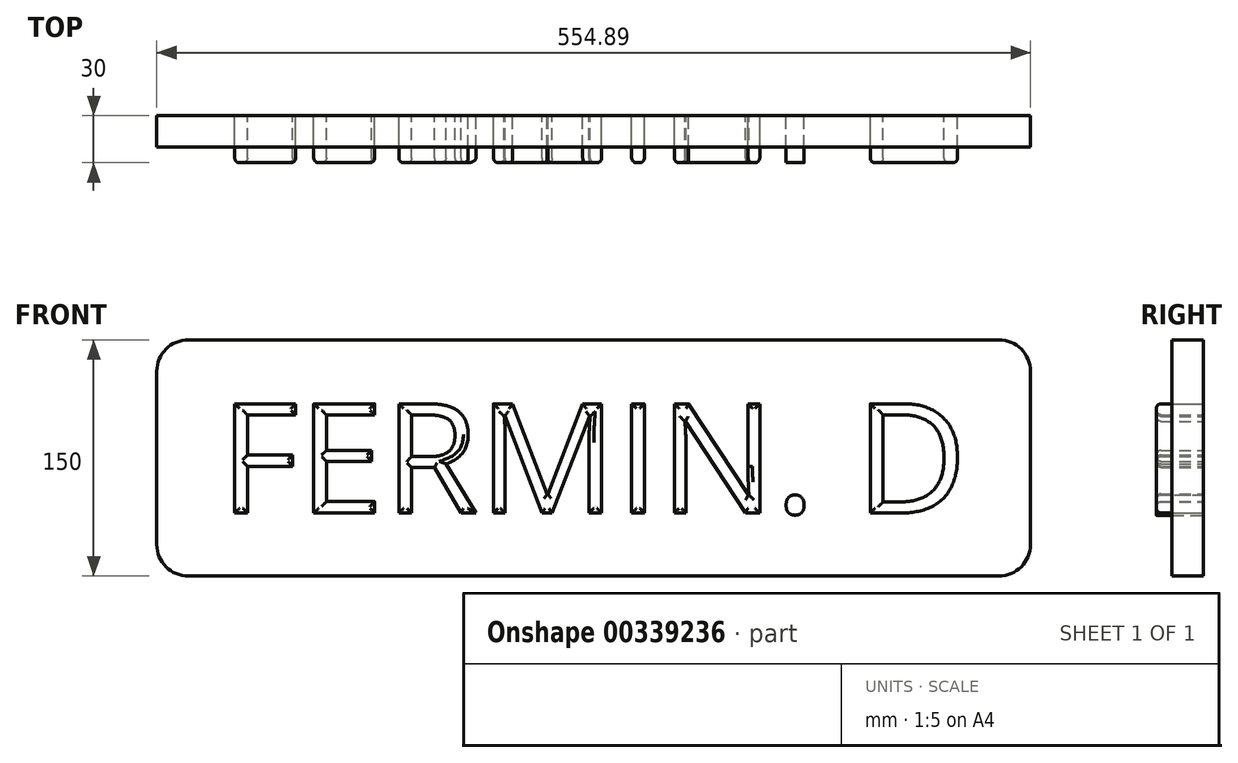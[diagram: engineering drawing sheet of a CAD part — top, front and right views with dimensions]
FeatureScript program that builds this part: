
annotation { "Feature Type Name" : "Feature", "Feature Type Description" : "" }
export const myFeature = defineFeature(function(context is Context, id is Id, definition is map)
    precondition{}
    {
        {
            var Q0;
            Q0=qCreatedBy(makeId("Front.planeOp"),FACE);
            var sketch = newSketch(context, id + "F0", { "sketchPlane" : qUnion([Q0])});
            skText(sketch, "E0", { "text": "FERMIN. D", "fontName": "OpenSans-Regular.ttf"});
            const initialGuessF0  = {"E0": [0.29518, 0.37068, 1, 0, 0.07]};
            skSetInitialGuess(sketch, initialGuessF0);
            skSolve(sketch);
        }
        {
            var Q0;
            Q0=qCreatedBy(makeId("Front.planeOp"),FACE);
            var sketch = newSketch(context, id + "F1", { "sketchPlane" : qUnion([Q0])});
            skLineSegment(sketch, "E1.0", {"start": v(295.18, 440.68) * mm, "end": v(770.07, 440.68) * mm, "construction": true});
            skLineSegment(sketch, "E2.0", {"start": v(295.18, 370.68) * mm, "end": v(770.07, 370.68) * mm, "construction": true});
            skLineSegment(sketch, "E3.0", {"start": v(770.07, 370.68) * mm, "end": v(770.07, 440.68) * mm, "construction": true});
            skLineSegment(sketch, "E4.0", {"start": v(295.18, 370.68) * mm, "end": v(295.18, 440.68) * mm, "construction": true});
            skLineSegment(sketch, "E5.0", {"start": v(275.18, 480.68) * mm, "end": v(790.07, 480.68) * mm});
            skLineSegment(sketch, "E5.1", {"start": v(255.18, 350.68) * mm, "end": v(255.18, 460.68) * mm});
            skLineSegment(sketch, "E5.2", {"start": v(275.18, 330.68) * mm, "end": v(790.07, 330.68) * mm});
            skLineSegment(sketch, "E5.3", {"start": v(810.07, 350.68) * mm, "end": v(810.07, 460.68) * mm});
            skPoint(sketch, "E6.visualSharp", {"position": v(255.18, 480.68) * mm});
            skArc(sketch, "E6.filletArc", {"start": v(275.18, 480.68) * mm, "mid": v(261.04, 474.82) * mm, "end": v(255.18, 460.68) * mm});
            skPoint(sketch, "E7.visualSharp", {"position": v(810.07, 480.68) * mm});
            skArc(sketch, "E7.filletArc", {"start": v(810.07, 460.68) * mm, "mid": v(804.21, 474.82) * mm, "end": v(790.07, 480.68) * mm});
            skPoint(sketch, "E8.visualSharp", {"position": v(810.07, 330.68) * mm});
            skArc(sketch, "E8.filletArc", {"start": v(790.07, 330.68) * mm, "mid": v(804.21, 336.53) * mm, "end": v(810.07, 350.68) * mm});
            skPoint(sketch, "E9.visualSharp", {"position": v(255.18, 330.68) * mm});
            skArc(sketch, "E9.filletArc", {"start": v(255.18, 350.68) * mm, "mid": v(261.04, 336.53) * mm, "end": v(275.18, 330.68) * mm});
            skSolve(sketch);
        }
        {
            var Q0;
            Q0 = qSketchRegion(id + "F0", true);
            extrude(context, id + "F2", {"entities" : qUnion([Q0]), "depth" : 30 * mm});
        }
        {
            var Q0;
            Q0=makeQuery(id+"F1.imprint","IMPRINT",FACE,{"disambiguationData":[TD([[makeQuery(id+"F1.imprint","IMPRINT",EDGE,{"derivedFrom":sQuery(id+"F1.wireOp",EDGE,"E5.0")}),-1.0]])]});
            extrude(context, id + "F3", {"entities" : qUnion([Q0]), "depth" : 20 * mm});
        }
        {
            var Q0;
            Q0=makeQuery(id+"F2.opExtrude","CAP_FACE",FACE,{"disambiguationData":[OSD([sQuery(id+"F0.wireOp",EDGE,"E0.sketch_text.stroke-0"),sQuery(id+"F0.wireOp",EDGE,"E0.sketch_text.stroke-1"),sQuery(id+"F0.wireOp",EDGE,"E0.sketch_text.stroke-2"),sQuery(id+"F0.wireOp",EDGE,"E0.sketch_text.stroke-3"),sQuery(id+"F0.wireOp",EDGE,"E0.sketch_text.stroke-4"),sQuery(id+"F0.wireOp",EDGE,"E0.sketch_text.stroke-5"),sQuery(id+"F0.wireOp",EDGE,"E0.sketch_text.stroke-6"),sQuery(id+"F0.wireOp",EDGE,"E0.sketch_text.stroke-7"),sQuery(id+"F0.wireOp",EDGE,"E0.sketch_text.stroke-8"),sQuery(id+"F0.wireOp",EDGE,"E0.sketch_text.stroke-9")])],"isStart":false});
            var Q1;
            Q1=makeQuery(id+"F2.opExtrude","CAP_FACE",FACE,{"disambiguationData":[OSD([sQuery(id+"F0.wireOp",EDGE,"E0.sketch_text.stroke-10"),sQuery(id+"F0.wireOp",EDGE,"E0.sketch_text.stroke-11"),sQuery(id+"F0.wireOp",EDGE,"E0.sketch_text.stroke-12"),sQuery(id+"F0.wireOp",EDGE,"E0.sketch_text.stroke-13"),sQuery(id+"F0.wireOp",EDGE,"E0.sketch_text.stroke-14"),sQuery(id+"F0.wireOp",EDGE,"E0.sketch_text.stroke-15"),sQuery(id+"F0.wireOp",EDGE,"E0.sketch_text.stroke-16"),sQuery(id+"F0.wireOp",EDGE,"E0.sketch_text.stroke-17"),sQuery(id+"F0.wireOp",EDGE,"E0.sketch_text.stroke-18"),sQuery(id+"F0.wireOp",EDGE,"E0.sketch_text.stroke-19"),sQuery(id+"F0.wireOp",EDGE,"E0.sketch_text.stroke-20"),sQuery(id+"F0.wireOp",EDGE,"E0.sketch_text.stroke-21")])],"isStart":false});
            var Q2;
            Q2=makeQuery(id+"F2.opExtrude","CAP_FACE",FACE,{"disambiguationData":[OSD([sQuery(id+"F0.wireOp",EDGE,"E0.sketch_text.stroke-22"),sQuery(id+"F0.wireOp",EDGE,"E0.sketch_text.stroke-23"),sQuery(id+"F0.wireOp",EDGE,"E0.sketch_text.stroke-24"),sQuery(id+"F0.wireOp",EDGE,"E0.sketch_text.stroke-25"),sQuery(id+"F0.wireOp",EDGE,"E0.sketch_text.stroke-26"),sQuery(id+"F0.wireOp",EDGE,"E0.sketch_text.stroke-27"),sQuery(id+"F0.wireOp",EDGE,"E0.sketch_text.stroke-28"),sQuery(id+"F0.wireOp",EDGE,"E0.sketch_text.stroke-29"),sQuery(id+"F0.wireOp",EDGE,"E0.sketch_text.stroke-30"),sQuery(id+"F0.wireOp",EDGE,"E0.sketch_text.stroke-31"),sQuery(id+"F0.wireOp",EDGE,"E0.sketch_text.stroke-32"),sQuery(id+"F0.wireOp",EDGE,"E0.sketch_text.stroke-33"),sQuery(id+"F0.wireOp",EDGE,"E0.sketch_text.stroke-34"),sQuery(id+"F0.wireOp",EDGE,"E0.sketch_text.stroke-35"),sQuery(id+"F0.wireOp",EDGE,"E0.sketch_text.stroke-36"),sQuery(id+"F0.wireOp",EDGE,"E0.sketch_text.stroke-37"),sQuery(id+"F0.wireOp",EDGE,"E0.sketch_text.stroke-38"),sQuery(id+"F0.wireOp",EDGE,"E0.sketch_text.stroke-39")])],"isStart":false});
            var Q3;
            Q3=makeQuery(id+"F2.opExtrude","CAP_FACE",FACE,{"disambiguationData":[OSD([sQuery(id+"F0.wireOp",EDGE,"E0.sketch_text.stroke-40"),sQuery(id+"F0.wireOp",EDGE,"E0.sketch_text.stroke-41"),sQuery(id+"F0.wireOp",EDGE,"E0.sketch_text.stroke-42"),sQuery(id+"F0.wireOp",EDGE,"E0.sketch_text.stroke-43"),sQuery(id+"F0.wireOp",EDGE,"E0.sketch_text.stroke-44"),sQuery(id+"F0.wireOp",EDGE,"E0.sketch_text.stroke-45"),sQuery(id+"F0.wireOp",EDGE,"E0.sketch_text.stroke-46"),sQuery(id+"F0.wireOp",EDGE,"E0.sketch_text.stroke-47"),sQuery(id+"F0.wireOp",EDGE,"E0.sketch_text.stroke-48"),sQuery(id+"F0.wireOp",EDGE,"E0.sketch_text.stroke-49"),sQuery(id+"F0.wireOp",EDGE,"E0.sketch_text.stroke-50"),sQuery(id+"F0.wireOp",EDGE,"E0.sketch_text.stroke-51"),sQuery(id+"F0.wireOp",EDGE,"E0.sketch_text.stroke-52"),sQuery(id+"F0.wireOp",EDGE,"E0.sketch_text.stroke-53"),sQuery(id+"F0.wireOp",EDGE,"E0.sketch_text.stroke-54"),sQuery(id+"F0.wireOp",EDGE,"E0.sketch_text.stroke-55"),sQuery(id+"F0.wireOp",EDGE,"E0.sketch_text.stroke-56"),sQuery(id+"F0.wireOp",EDGE,"E0.sketch_text.stroke-57")])],"isStart":false});
            var Q4;
            Q4=makeQuery(id+"F2.opExtrude","CAP_FACE",FACE,{"disambiguationData":[OSD([sQuery(id+"F0.wireOp",EDGE,"E0.sketch_text.stroke-58"),sQuery(id+"F0.wireOp",EDGE,"E0.sketch_text.stroke-59"),sQuery(id+"F0.wireOp",EDGE,"E0.sketch_text.stroke-60"),sQuery(id+"F0.wireOp",EDGE,"E0.sketch_text.stroke-61")])],"isStart":false});
            var Q5;
            Q5=makeQuery(id+"F2.opExtrude","CAP_FACE",FACE,{"disambiguationData":[OSD([sQuery(id+"F0.wireOp",EDGE,"E0.sketch_text.stroke-62"),sQuery(id+"F0.wireOp",EDGE,"E0.sketch_text.stroke-63"),sQuery(id+"F0.wireOp",EDGE,"E0.sketch_text.stroke-64"),sQuery(id+"F0.wireOp",EDGE,"E0.sketch_text.stroke-65"),sQuery(id+"F0.wireOp",EDGE,"E0.sketch_text.stroke-66"),sQuery(id+"F0.wireOp",EDGE,"E0.sketch_text.stroke-67"),sQuery(id+"F0.wireOp",EDGE,"E0.sketch_text.stroke-68"),sQuery(id+"F0.wireOp",EDGE,"E0.sketch_text.stroke-69"),sQuery(id+"F0.wireOp",EDGE,"E0.sketch_text.stroke-70"),sQuery(id+"F0.wireOp",EDGE,"E0.sketch_text.stroke-71"),sQuery(id+"F0.wireOp",EDGE,"E0.sketch_text.stroke-72"),sQuery(id+"F0.wireOp",EDGE,"E0.sketch_text.stroke-73"),sQuery(id+"F0.wireOp",EDGE,"E0.sketch_text.stroke-74"),sQuery(id+"F0.wireOp",EDGE,"E0.sketch_text.stroke-75"),sQuery(id+"F0.wireOp",EDGE,"E0.sketch_text.stroke-76")])],"isStart":false});
            var Q6;
            Q6=makeQuery(id+"F2.opExtrude","CAP_FACE",FACE,{"disambiguationData":[OSD([sQuery(id+"F0.wireOp",EDGE,"E0.sketch_text.stroke-85"),sQuery(id+"F0.wireOp",EDGE,"E0.sketch_text.stroke-86"),sQuery(id+"F0.wireOp",EDGE,"E0.sketch_text.stroke-87"),sQuery(id+"F0.wireOp",EDGE,"E0.sketch_text.stroke-88"),sQuery(id+"F0.wireOp",EDGE,"E0.sketch_text.stroke-89"),sQuery(id+"F0.wireOp",EDGE,"E0.sketch_text.stroke-90"),sQuery(id+"F0.wireOp",EDGE,"E0.sketch_text.stroke-91"),sQuery(id+"F0.wireOp",EDGE,"E0.sketch_text.stroke-92"),sQuery(id+"F0.wireOp",EDGE,"E0.sketch_text.stroke-93"),sQuery(id+"F0.wireOp",EDGE,"E0.sketch_text.stroke-94"),sQuery(id+"F0.wireOp",EDGE,"E0.sketch_text.stroke-95"),sQuery(id+"F0.wireOp",EDGE,"E0.sketch_text.stroke-96"),sQuery(id+"F0.wireOp",EDGE,"E0.sketch_text.stroke-97"),sQuery(id+"F0.wireOp",EDGE,"E0.sketch_text.stroke-98")])],"isStart":false});
            fillet(context, id + "F4", {"entities" : qUnion([Q0, Q1, Q2, Q3, Q4, Q5, Q6]), "radius" : 3 * mm, "tangentPropagation" : true, "allowEdgeOverflow" : false});
        }
    });
